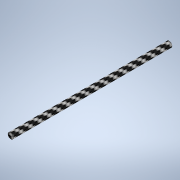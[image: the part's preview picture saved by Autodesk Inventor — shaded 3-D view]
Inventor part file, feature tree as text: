
AUTODESK INVENTOR PART (.ipt)
format: ipt  version: 2020 (Build 240168000, 168)  size: 107,520 bytes
history: native  units: in
note: dims shown in document units (in); Inventor stores cm internally (conversion verified against a paired STEP export)
features: extrude x1, sketch x1
ambient origin geometry x8: Origin, YZ Plane, XZ Plane, XY Plane, X Axis, Y Axis, Z Axis, Center Point
bodies: Solid1 (feature_tree)
feature tree (2):
  extrude  "Extrusion1"  Depth=2.4807in
  sketch  "Sketch1"  dims[d0=0.0906in d1=2.4807in d2=0.0in]
